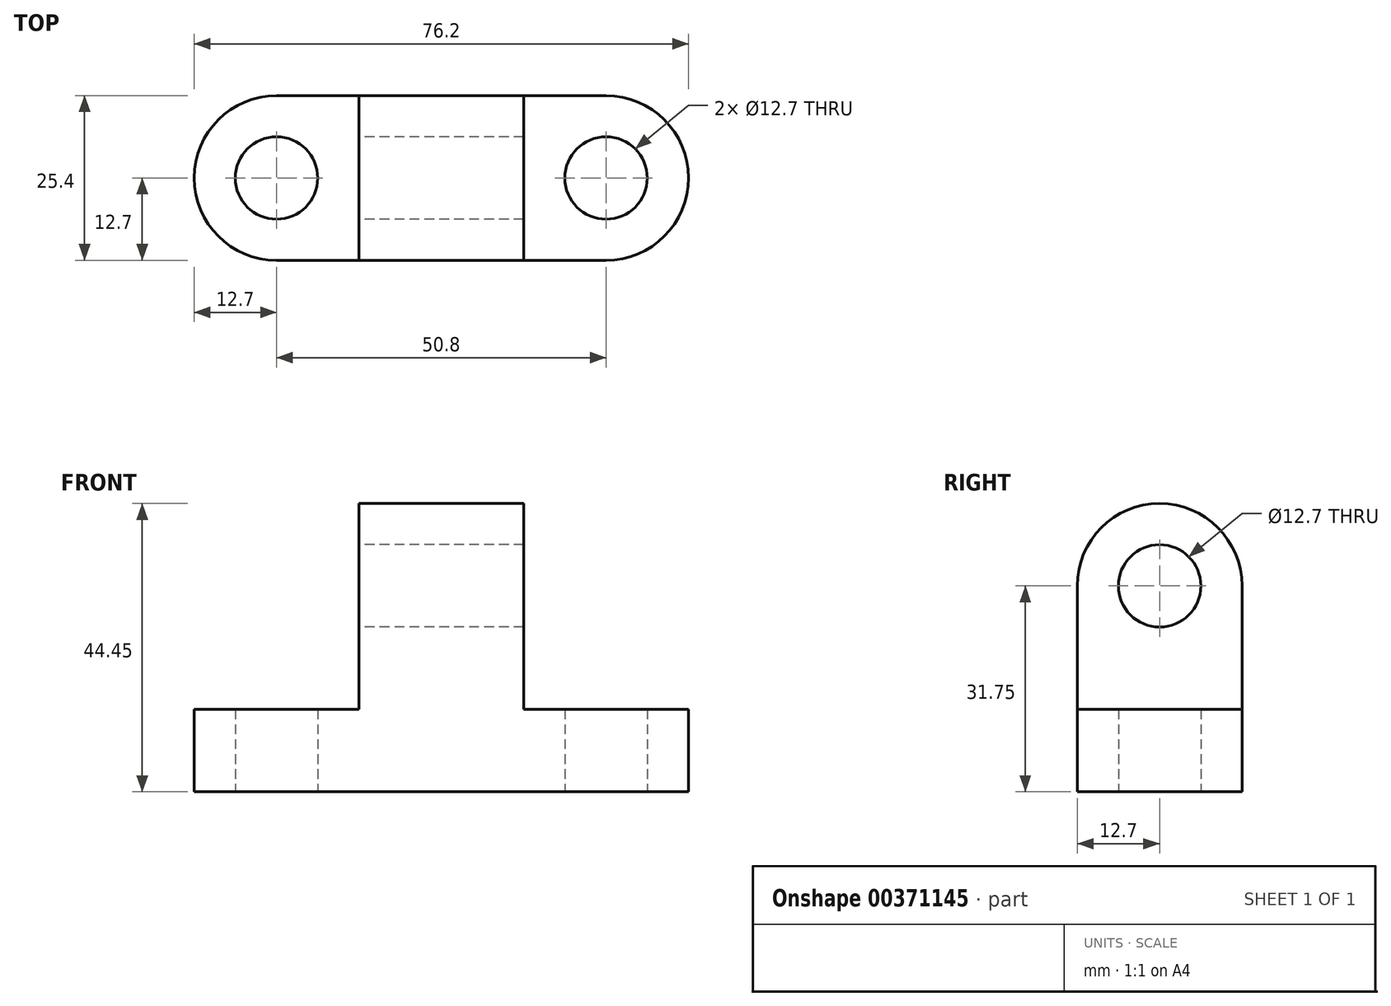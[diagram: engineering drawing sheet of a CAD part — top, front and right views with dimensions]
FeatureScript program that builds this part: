
annotation { "Feature Type Name" : "Feature", "Feature Type Description" : "" }
export const myFeature = defineFeature(function(context is Context, id is Id, definition is map)
    precondition{}
    {
        {
            var Q0;
            Q0=qCreatedBy(makeId("Front.planeOp"),FACE);
            var sketch = newSketch(context, id + "F0", { "sketchPlane" : qUnion([Q0])});
            skLineSegment(sketch, "E0", {"start": v(0, 0) * mm, "end": v(0, 44.45) * mm});
            skLineSegment(sketch, "E1", {"start": v(0, 44.45) * mm, "end": v(25.4, 44.45) * mm});
            skLineSegment(sketch, "E2", {"start": v(25.4, 44.45) * mm, "end": v(25.4, 0) * mm});
            skLineSegment(sketch, "E3", {"start": v(25.4, 0) * mm, "end": v(0, 0) * mm});
            skSolve(sketch);
        }
        {
            var Q0;
            Q0 = qSketchRegion(id + "F0", true);
            extrude(context, id + "F1", {"entities" : qUnion([Q0]), "oppositeDirection" : true, "depth" : 25.4 * mm});
        }
        {
            var Q0;
            Q0=makeQuery(id+"F1.opExtrude","CAP_EDGE",EDGE,{"disambiguationData":[OSD([sQuery(id+"F0.wireOp",EDGE,"E1")])],"isStart":true});
            var Q1;
            Q1=makeQuery(id+"F1.opExtrude","CAP_EDGE",EDGE,{"disambiguationData":[OSD([sQuery(id+"F0.wireOp",EDGE,"E1")])],"isStart":false});
            fillet(context, id + "F2", {"entities" : qUnion([Q0, Q1]), "radius" : 12.7 * mm, "tangentPropagation" : true, "allowEdgeOverflow" : false});
        }
        {
            var Q0;
            Q0=makeQuery(id+"F1.opExtrude","SWEPT_FACE",FACE,{"disambiguationData":[OSD([sQuery(id+"F0.wireOp",EDGE,"E2")])]});
            var sketch = newSketch(context, id + "F3", { "sketchPlane" : qUnion([Q0])});
            skSolve(sketch);
        }
        {
            var Q0;
            Q0=qCreatedBy(makeId("Right.planeOp"),FACE);
            var sketch = newSketch(context, id + "F4", { "sketchPlane" : qUnion([Q0])});
            skLineSegment(sketch, "E4.0.0", {"start": v(25.4, 0) * mm, "end": v(25.4, 31.75) * mm});
            skArc(sketch, "E4.0.1", {"start": v(25.4, 31.75) * mm, "mid": v(12.7, 44.45) * mm, "end": v(0, 31.75) * mm});
            skLineSegment(sketch, "E4.0.2", {"start": v(0, 31.75) * mm, "end": v(0, 0) * mm});
            skLineSegment(sketch, "E4.0.3", {"start": v(0, 0) * mm, "end": v(25.4, 0) * mm});
            skCircle(sketch, "E5", {"center": v(12.7, 31.75) * mm, "radius": 6.35 * mm});
            skSolve(sketch);
        }
        {
            var Q0;
            Q0=makeQuery(id+"F4.imprint","IMPRINT",FACE,{"disambiguationData":[TD([[makeQuery(id+"F4.imprint","IMPRINT",EDGE,{"derivedFrom":sQuery(id+"F4.wireOp",EDGE,"E5")}),1.0]])]});
            extrude(context, id + "F5", {"entities" : qUnion([Q0]), "operationType" : NewBodyOperationType.REMOVE, "depth" : 25.4 * mm});
        }
        {
            var Q0;
            Q0=qCreatedBy(makeId("Top.planeOp"),FACE);
            var sketch = newSketch(context, id + "F6", { "sketchPlane" : qUnion([Q0])});
            skLineSegment(sketch, "E6.bottom", {"start": v(0, 0) * mm, "end": v(-25.4, 0) * mm});
            skLineSegment(sketch, "E6.top", {"start": v(0, 25.4) * mm, "end": v(-25.4, 25.4) * mm});
            skLineSegment(sketch, "E6.left", {"start": v(0, 0) * mm, "end": v(0, 25.4) * mm});
            skLineSegment(sketch, "E6.right", {"start": v(-25.4, 0) * mm, "end": v(-25.4, 25.4) * mm});
            skLineSegment(sketch, "E7.0.0", {"start": v(25.4, 0) * mm, "end": v(0, 0) * mm});
            skLineSegment(sketch, "E7.0.2", {"start": v(0, 25.4) * mm, "end": v(25.4, 25.4) * mm});
            skLineSegment(sketch, "E7.0.3", {"start": v(25.4, 25.4) * mm, "end": v(25.4, 0) * mm});
            skLineSegment(sketch, "E8.bottom", {"start": v(25.4, 0) * mm, "end": v(50.8, 0) * mm});
            skLineSegment(sketch, "E8.top", {"start": v(25.4, 25.4) * mm, "end": v(50.8, 25.4) * mm});
            skLineSegment(sketch, "E8.left", {"start": v(25.4, 0) * mm, "end": v(25.4, 25.4) * mm});
            skLineSegment(sketch, "E8.right", {"start": v(50.8, 0) * mm, "end": v(50.8, 25.4) * mm});
            skSolve(sketch);
        }
        {
            var Q0;
            Q0=makeQuery(id+"F6.imprint","IMPRINT",FACE,{"disambiguationData":[TD([[makeQuery(id+"F6.imprint","IMPRINT",EDGE,{"derivedFrom":sQuery(id+"F6.wireOp",EDGE,"E6.bottom")}),-1.0]])]});
            var Q1;
            Q1=makeQuery(id+"F6.imprint","IMPRINT",FACE,{"disambiguationData":[TD([[makeQuery(id+"F6.imprint","IMPRINT",EDGE,{"derivedFrom":sQuery(id+"F6.wireOp",EDGE,"E8.bottom")}),1.0]])]});
            extrude(context, id + "F7", {"entities" : qUnion([Q0, Q1]), "operationType" : NewBodyOperationType.ADD, "depth" : 12.7 * mm});
        }
        {
            var Q0;
            Q0=makeQuery(id+"F7.opExtrude","SWEPT_EDGE",EDGE,{"disambiguationData":[OSD([sQuery(id+"F6.wireOp",EDGE,"E6.top"),sQuery(id+"F6.wireOp",EDGE,"E6.right")])]});
            var Q1;
            Q1=makeQuery(id+"F7.opExtrude","SWEPT_EDGE",EDGE,{"disambiguationData":[OSD([sQuery(id+"F6.wireOp",EDGE,"E6.bottom"),sQuery(id+"F6.wireOp",EDGE,"E6.right")])]});
            fillet(context, id + "F8", {"entities" : qUnion([Q0, Q1]), "radius" : 12.7 * mm, "tangentPropagation" : true, "allowEdgeOverflow" : false});
        }
        {
            var Q0;
            Q0=makeQuery(id+"F7.opExtrude","SWEPT_EDGE",EDGE,{"disambiguationData":[OSD([sQuery(id+"F6.wireOp",EDGE,"E8.bottom"),sQuery(id+"F6.wireOp",EDGE,"E8.right")])]});
            var Q1;
            Q1=makeQuery(id+"F7.opExtrude","SWEPT_EDGE",EDGE,{"disambiguationData":[OSD([sQuery(id+"F6.wireOp",EDGE,"E8.top"),sQuery(id+"F6.wireOp",EDGE,"E8.right")])]});
            fillet(context, id + "F9", {"entities" : qUnion([Q0, Q1]), "radius" : 12.7 * mm, "tangentPropagation" : true, "allowEdgeOverflow" : false});
        }
        {
            var Q0;
            Q0=qCreatedBy(makeId("Top.planeOp"),FACE);
            var sketch = newSketch(context, id + "F10", { "sketchPlane" : qUnion([Q0])});
            skArc(sketch, "E9.0.0", {"start": v(-12.7, 25.4) * mm, "mid": v(-25.4, 12.7) * mm, "end": v(-12.7, 0) * mm});
            skLineSegment(sketch, "E9.0.1", {"start": v(-12.7, 0) * mm, "end": v(0, 0) * mm});
            skLineSegment(sketch, "E9.0.2", {"start": v(0, 0) * mm, "end": v(0, 25.4) * mm});
            skLineSegment(sketch, "E9.0.3", {"start": v(0, 25.4) * mm, "end": v(-12.7, 25.4) * mm});
            skCircle(sketch, "E10", {"center": v(-12.7, 12.7) * mm, "radius": 6.35 * mm});
            skSolve(sketch);
        }
        {
            var Q0;
            Q0=makeQuery(id+"F10.imprint","IMPRINT",FACE,{"disambiguationData":[TD([[makeQuery(id+"F10.imprint","IMPRINT",EDGE,{"derivedFrom":sQuery(id+"F10.wireOp",EDGE,"E10")}),1.0]])]});
            extrude(context, id + "F11", {"entities" : qUnion([Q0]), "operationType" : NewBodyOperationType.REMOVE, "depth" : 12.7 * mm});
        }
        {
            var Q0;
            Q0=qCreatedBy(makeId("Top.planeOp"),FACE);
            var sketch = newSketch(context, id + "F12", { "sketchPlane" : qUnion([Q0])});
            skLineSegment(sketch, "E11.0.0", {"start": v(25.4, 0) * mm, "end": v(38.1, 0) * mm});
            skArc(sketch, "E11.0.1", {"start": v(38.1, 0) * mm, "mid": v(50.8, 12.7) * mm, "end": v(38.1, 25.4) * mm});
            skLineSegment(sketch, "E11.0.2", {"start": v(38.1, 25.4) * mm, "end": v(25.4, 25.4) * mm});
            skLineSegment(sketch, "E11.0.3", {"start": v(25.4, 25.4) * mm, "end": v(25.4, 0) * mm});
            skCircle(sketch, "E12", {"center": v(38.1, 12.7) * mm, "radius": 6.35 * mm});
            skSolve(sketch);
        }
        {
            var Q0;
            Q0=makeQuery(id+"F12.imprint","IMPRINT",FACE,{"disambiguationData":[TD([[makeQuery(id+"F12.imprint","IMPRINT",EDGE,{"derivedFrom":sQuery(id+"F12.wireOp",EDGE,"E12")}),1.0]])]});
            extrude(context, id + "F13", {"entities" : qUnion([Q0]), "operationType" : NewBodyOperationType.REMOVE, "depth" : 12.7 * mm});
        }
    });
